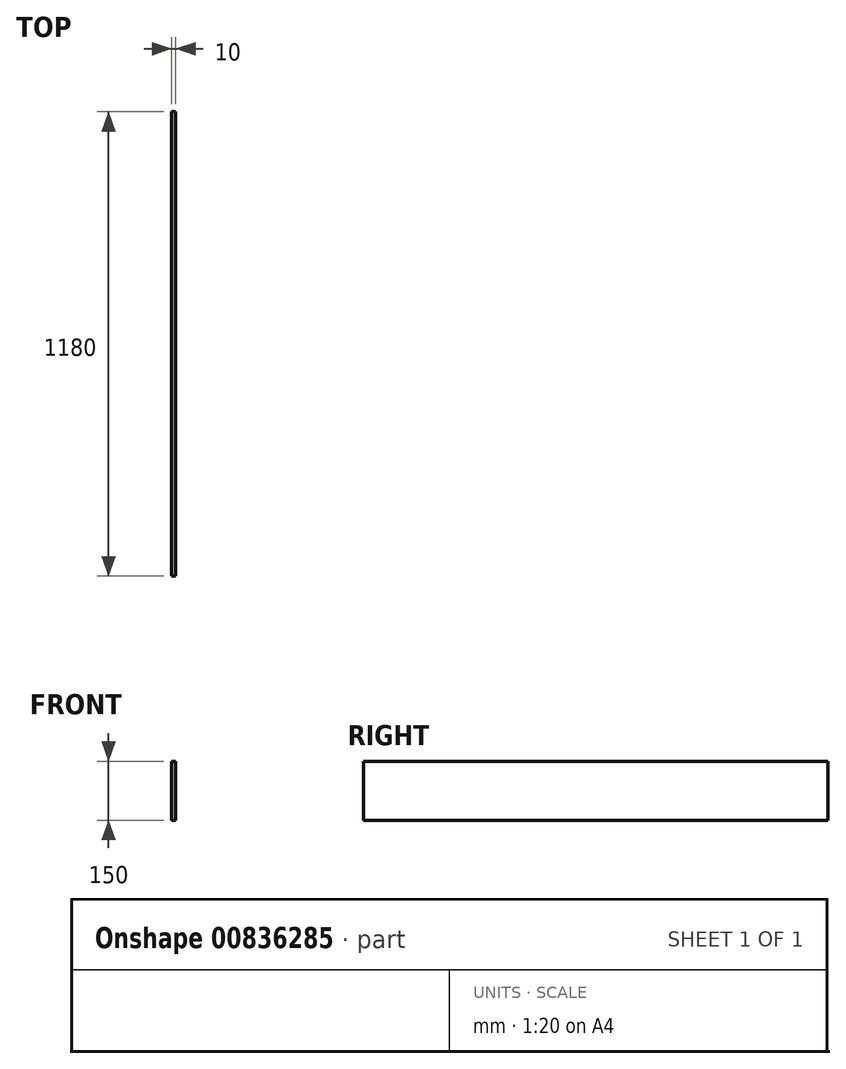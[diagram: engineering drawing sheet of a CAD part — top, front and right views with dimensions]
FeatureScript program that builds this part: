
annotation { "Feature Type Name" : "Feature", "Feature Type Description" : "" }
export const myFeature = defineFeature(function(context is Context, id is Id, definition is map)
    precondition{}
    {
        {
            var Q0;
            Q0=qCreatedBy(makeId("Right.planeOp"),FACE);
            var sketch = newSketch(context, id + "F0", { "sketchPlane" : qUnion([Q0])});
            skLineSegment(sketch, "E0.bottom", {"start": v(0, 0) * mm, "end": v(1180, 0) * mm});
            skLineSegment(sketch, "E0.top", {"start": v(0, 150) * mm, "end": v(1180, 150) * mm});
            skLineSegment(sketch, "E0.left", {"start": v(0, 0) * mm, "end": v(0, 150) * mm});
            skLineSegment(sketch, "E0.right", {"start": v(1180, 0) * mm, "end": v(1180, 150) * mm});
            skSolve(sketch);
        }
        {
            var Q0;
            Q0=makeQuery(id+"F0.imprint","IMPRINT",FACE,{"disambiguationData":[TD([[makeQuery(id+"F0.imprint","IMPRINT",EDGE,{"derivedFrom":sQuery(id+"F0.wireOp",EDGE,"E0.bottom")}),1.0]])]});
            extrude(context, id + "F1", {"entities" : qUnion([Q0]), "depth" : 10 * mm, "offsetDistance" : 25 * mm});
        }
    });
